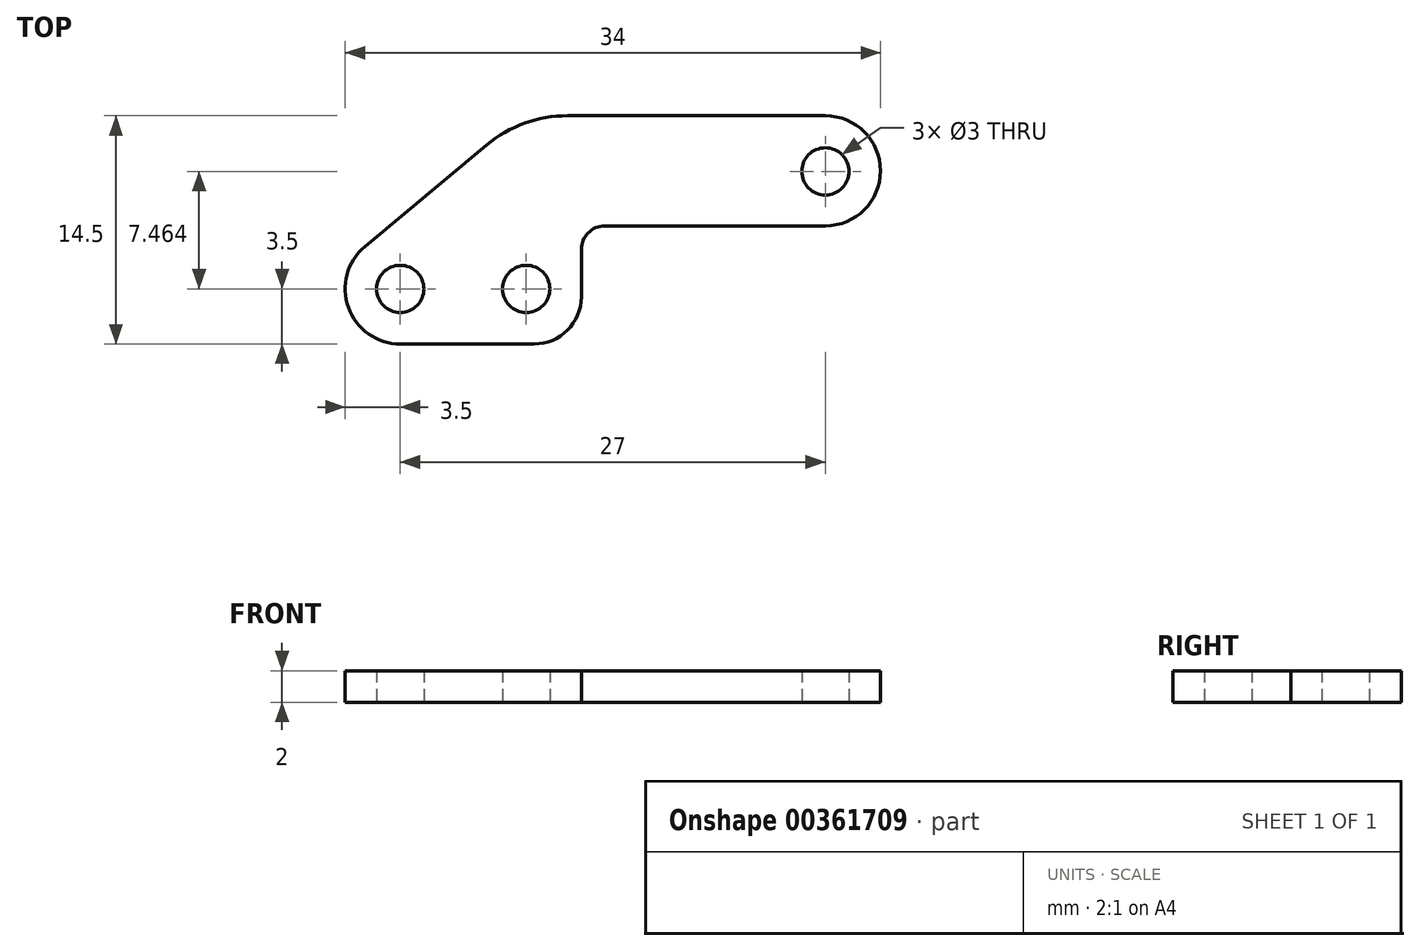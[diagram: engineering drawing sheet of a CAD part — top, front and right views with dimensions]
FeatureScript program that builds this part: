
annotation { "Feature Type Name" : "Feature", "Feature Type Description" : "" }
export const myFeature = defineFeature(function(context is Context, id is Id, definition is map)
    precondition{}
    {
        {
            var Q0;
            Q0=qCreatedBy(makeId("Top.planeOp"),FACE);
            var sketch = newSketch(context, id + "F0", { "sketchPlane" : qUnion([Q0])});
            skLineSegment(sketch, "E0.bottom", {"start": v(4.5, -3.5) * mm, "end": v(-4, -3.5) * mm});
            skLineSegment(sketch, "E0.right", {"start": v(-7.5, 0) * mm, "end": v(-7.5, 0) * mm});
            skPoint(sketch, "E0.middle", {"position": v(0, 0) * mm});
            skCircle(sketch, "E1", {"center": v(4, 0) * mm, "radius": 1.5 * mm});
            skCircle(sketch, "E2", {"center": v(-4, 0) * mm, "radius": 1.5 * mm});
            skPoint(sketch, "E3.visualSharp", {"position": v(-7.5, 3.5) * mm});
            skPoint(sketch, "E4.visualSharp", {"position": v(-7.5, -3.5) * mm});
            skArc(sketch, "E4.filletArc", {"start": v(-7.5, 0) * mm, "mid": v(-6.47, -2.47) * mm, "end": v(-4, -3.5) * mm});
            skPoint(sketch, "E5.visualSharp", {"position": v(7.5, -3.5) * mm});
            skLineSegment(sketch, "E6", {"start": v(7.5, -0.5) * mm, "end": v(7.5, 2.5) * mm});
            skPoint(sketch, "E7.visualSharp", {"position": v(0.5, 3.5) * mm});
            skPoint(sketch, "E8.visualSharp", {"position": v(0.5, 11) * mm});
            skPoint(sketch, "E9.visualSharp", {"position": v(26.5, 11) * mm});
            skCircle(sketch, "E10", {"center": v(23, 7.46) * mm, "radius": 1.5 * mm});
            skArc(sketch, "E11.filletArc", {"start": v(4.5, -3.5) * mm, "mid": v(6.62, -2.62) * mm, "end": v(7.5, -0.5) * mm});
            skArc(sketch, "E12.filletArc", {"start": v(9, 4) * mm, "mid": v(7.94, 3.56) * mm, "end": v(7.5, 2.5) * mm});
            skLineSegment(sketch, "E13", {"start": v(26.5, 7.5) * mm, "end": v(26.5, 7.5) * mm});
            skLineSegment(sketch, "E14", {"start": v(9, 4) * mm, "end": v(23, 4) * mm});
            skPoint(sketch, "E15.visualSharp", {"position": v(26.5, 4) * mm});
            skArc(sketch, "E15.filletArc", {"start": v(23, 4) * mm, "mid": v(25.47, 5.03) * mm, "end": v(26.5, 7.5) * mm});
            skArc(sketch, "E16.filletArc", {"start": v(26.5, 7.5) * mm, "mid": v(25.47, 9.97) * mm, "end": v(23, 11) * mm});
            skLineSegment(sketch, "E17", {"start": v(-6.24, 2.69) * mm, "end": v(1.5, 9.14) * mm});
            skPoint(sketch, "E18.visualSharp", {"position": v(-7.5, 1.64) * mm});
            skArc(sketch, "E18.filletArc", {"start": v(-6.24, 2.69) * mm, "mid": v(-7.17, 1.48) * mm, "end": v(-7.5, 0) * mm});
            skLineSegment(sketch, "E19", {"start": v(6.62, 11) * mm, "end": v(23, 11) * mm});
            skPoint(sketch, "E20.visualSharp", {"position": v(3.72, 11) * mm});
            skArc(sketch, "E20.filletArc", {"start": v(6.62, 11) * mm, "mid": v(3.9, 10.52) * mm, "end": v(1.5, 9.14) * mm});
            skSolve(sketch);
        }
        {
            var Q0;
            Q0=makeQuery(id+"F0.imprint","IMPRINT",FACE,{"disambiguationData":[TD([[makeQuery(id+"F0.imprint","IMPRINT",EDGE,{"derivedFrom":sQuery(id+"F0.wireOp",EDGE,"E0.bottom")}),-1.0]])]});
            extrude(context, id + "F1", {"entities" : qUnion([Q0]), "depth" : 2 * mm});
        }
    });
